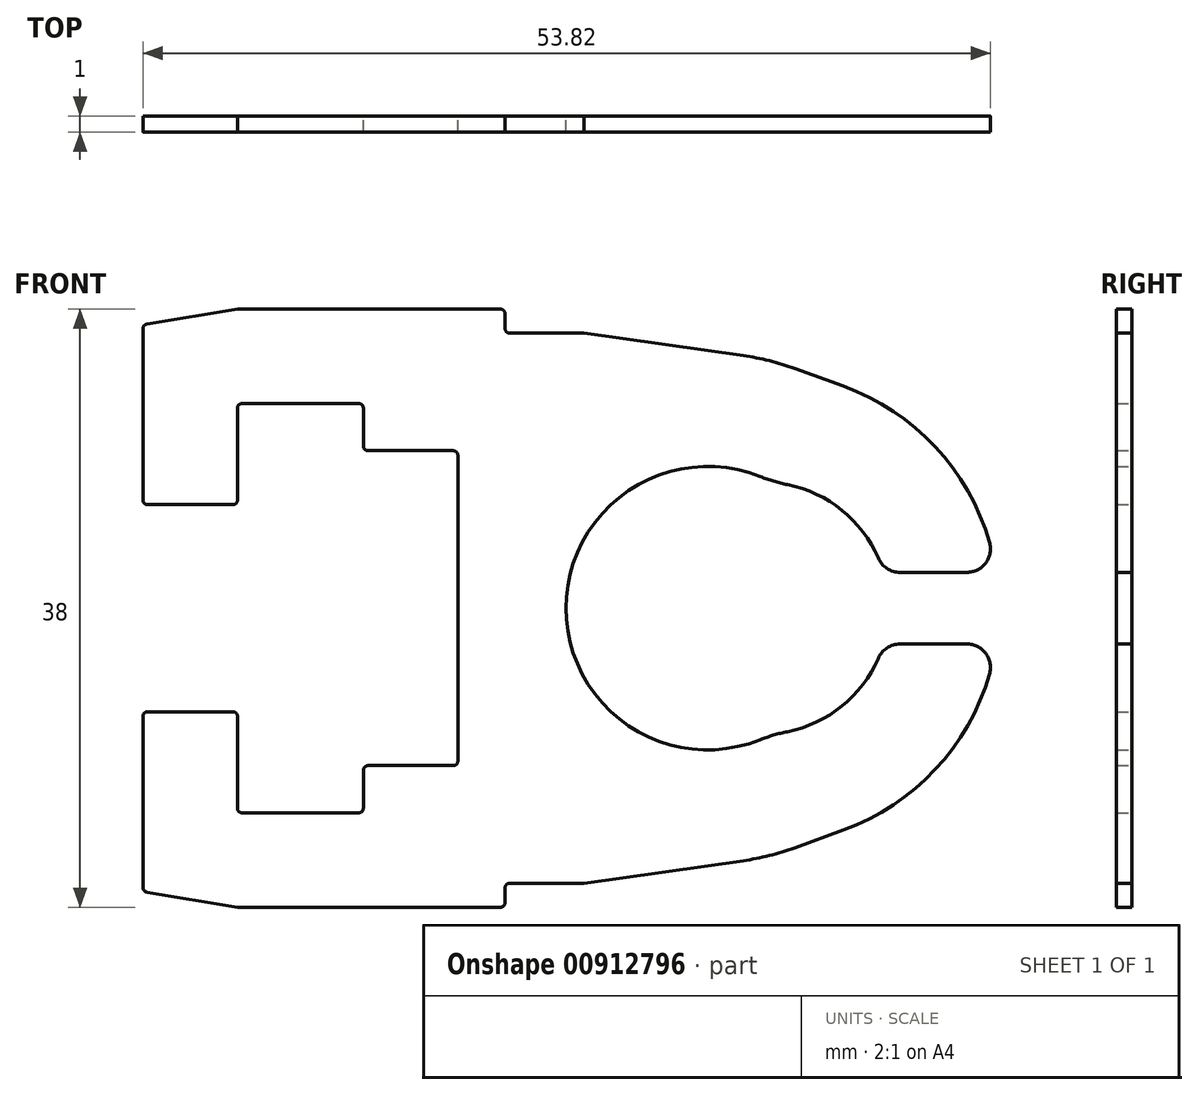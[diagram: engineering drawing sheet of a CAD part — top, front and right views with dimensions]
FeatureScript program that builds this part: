
annotation { "Feature Type Name" : "Feature", "Feature Type Description" : "" }
export const myFeature = defineFeature(function(context is Context, id is Id, definition is map)
    precondition{}
    {
        {
            var Q0;
            Q0=qCreatedBy(makeId("Front.planeOp"),FACE);
            var sketch = newSketch(context, id + "F0", { "sketchPlane" : qUnion([Q0])});
            skLineSegment(sketch, "E0", {"start": v(57.08, -14.1) * mm, "end": v(54, -15.22) * mm});
            skArc(sketch, "E1", {"start": v(50.71, -16.04) * mm, "mid": v(52.37, -15.72) * mm, "end": v(54, -15.22) * mm});
            skLineSegment(sketch, "E2", {"start": v(50.71, -16.04) * mm, "end": v(40.59, -17.47) * mm});
            skLineSegment(sketch, "E3", {"start": v(40.59, -17.47) * mm, "end": v(35.89, -17.47) * mm});
            skArc(sketch, "E4", {"start": v(35.89, -17.47) * mm, "mid": v(35.67, -17.55) * mm, "end": v(35.59, -17.77) * mm});
            skLineSegment(sketch, "E5", {"start": v(35.59, -17.77) * mm, "end": v(35.59, -18.7) * mm});
            skArc(sketch, "E6", {"start": v(35.29, -19) * mm, "mid": v(35.5, -18.91) * mm, "end": v(35.59, -18.7) * mm});
            skLineSegment(sketch, "E7", {"start": v(35.29, -19) * mm, "end": v(18.59, -19) * mm});
            skLineSegment(sketch, "E8", {"start": v(18.59, -19) * mm, "end": v(12.84, -18.04) * mm});
            skArc(sketch, "E9", {"start": v(12.59, -17.75) * mm, "mid": v(12.66, -17.94) * mm, "end": v(12.84, -18.04) * mm});
            skLineSegment(sketch, "E10", {"start": v(12.59, -17.75) * mm, "end": v(12.59, -6.87) * mm});
            skArc(sketch, "E11", {"start": v(12.89, -6.58) * mm, "mid": v(12.67, -6.66) * mm, "end": v(12.59, -6.88) * mm});
            skLineSegment(sketch, "E12", {"start": v(12.89, -6.58) * mm, "end": v(18.29, -6.58) * mm});
            skArc(sketch, "E13", {"start": v(18.59, -6.88) * mm, "mid": v(18.5, -6.66) * mm, "end": v(18.29, -6.58) * mm});
            skLineSegment(sketch, "E14", {"start": v(18.59, -6.88) * mm, "end": v(18.59, -12.7) * mm});
            skArc(sketch, "E15", {"start": v(18.59, -12.7) * mm, "mid": v(18.67, -12.91) * mm, "end": v(18.89, -13) * mm});
            skLineSegment(sketch, "E16", {"start": v(18.89, -13) * mm, "end": v(26.29, -13) * mm});
            skArc(sketch, "E17", {"start": v(26.29, -13) * mm, "mid": v(26.5, -12.91) * mm, "end": v(26.59, -12.7) * mm});
            skLineSegment(sketch, "E18", {"start": v(26.59, -12.7) * mm, "end": v(26.59, -10.3) * mm});
            skArc(sketch, "E19", {"start": v(26.89, -10) * mm, "mid": v(26.67, -10.09) * mm, "end": v(26.59, -10.3) * mm});
            skLineSegment(sketch, "E20", {"start": v(26.89, -10) * mm, "end": v(32.29, -10) * mm});
            skArc(sketch, "E21", {"start": v(32.29, -10) * mm, "mid": v(32.5, -9.91) * mm, "end": v(32.59, -9.7) * mm});
            skLineSegment(sketch, "E22", {"start": v(32.59, -9.7) * mm, "end": v(32.59, 9.7) * mm});
            skArc(sketch, "E23", {"start": v(32.59, 9.7) * mm, "mid": v(32.5, 9.91) * mm, "end": v(32.29, 10) * mm});
            skLineSegment(sketch, "E24", {"start": v(32.29, 10) * mm, "end": v(26.89, 10) * mm});
            skArc(sketch, "E25", {"start": v(26.59, 10.3) * mm, "mid": v(26.67, 10.09) * mm, "end": v(26.89, 10) * mm});
            skLineSegment(sketch, "E26", {"start": v(26.59, 10.3) * mm, "end": v(26.59, 12.7) * mm});
            skArc(sketch, "E27", {"start": v(26.59, 12.7) * mm, "mid": v(26.5, 12.91) * mm, "end": v(26.29, 13) * mm});
            skLineSegment(sketch, "E28", {"start": v(26.29, 13) * mm, "end": v(18.89, 13) * mm});
            skArc(sketch, "E29", {"start": v(18.89, 13) * mm, "mid": v(18.67, 12.91) * mm, "end": v(18.59, 12.7) * mm});
            skLineSegment(sketch, "E30", {"start": v(18.59, 12.7) * mm, "end": v(18.59, 6.88) * mm});
            skArc(sketch, "E31", {"start": v(18.29, 6.58) * mm, "mid": v(18.5, 6.66) * mm, "end": v(18.59, 6.88) * mm});
            skLineSegment(sketch, "E32", {"start": v(18.29, 6.57) * mm, "end": v(12.89, 6.57) * mm});
            skArc(sketch, "E33", {"start": v(12.59, 6.88) * mm, "mid": v(12.67, 6.66) * mm, "end": v(12.89, 6.58) * mm});
            skLineSegment(sketch, "E34", {"start": v(12.59, 6.88) * mm, "end": v(12.59, 17.75) * mm});
            skArc(sketch, "E35", {"start": v(12.84, 18.04) * mm, "mid": v(12.66, 17.94) * mm, "end": v(12.59, 17.75) * mm});
            skLineSegment(sketch, "E36", {"start": v(12.84, 18.04) * mm, "end": v(18.59, 19) * mm});
            skLineSegment(sketch, "E37", {"start": v(18.59, 19) * mm, "end": v(35.29, 19) * mm});
            skArc(sketch, "E38", {"start": v(35.59, 18.7) * mm, "mid": v(35.5, 18.91) * mm, "end": v(35.29, 19) * mm});
            skLineSegment(sketch, "E39", {"start": v(35.59, 18.7) * mm, "end": v(35.59, 17.76) * mm});
            skArc(sketch, "E40", {"start": v(35.59, 17.76) * mm, "mid": v(35.67, 17.55) * mm, "end": v(35.89, 17.46) * mm});
            skLineSegment(sketch, "E41", {"start": v(35.89, 17.46) * mm, "end": v(40.59, 17.46) * mm});
            skLineSegment(sketch, "E42", {"start": v(40.59, 17.46) * mm, "end": v(50.71, 16.04) * mm});
            skArc(sketch, "E43", {"start": v(54, 15.22) * mm, "mid": v(52.37, 15.72) * mm, "end": v(50.71, 16.04) * mm});
            skLineSegment(sketch, "E44", {"start": v(54, 15.22) * mm, "end": v(57.08, 14.1) * mm});
            skArc(sketch, "E45", {"start": v(66.35, 4.2) * mm, "mid": v(62.9, 10.25) * mm, "end": v(57.08, 14.1) * mm});
            skArc(sketch, "E46", {"start": v(64.91, 2.27) * mm, "mid": v(66.11, 2.87) * mm, "end": v(66.35, 4.2) * mm});
            skLineSegment(sketch, "E47", {"start": v(64.91, 2.27) * mm, "end": v(60.67, 2.27) * mm});
            skArc(sketch, "E48", {"start": v(59.3, 3.18) * mm, "mid": v(59.85, 2.52) * mm, "end": v(60.67, 2.27) * mm});
            skArc(sketch, "E49", {"start": v(59.3, 3.18) * mm, "mid": v(56.98, 6.22) * mm, "end": v(53.52, 7.84) * mm});
            skArc(sketch, "E50", {"start": v(51.79, 8.36) * mm, "mid": v(52.64, 8.06) * mm, "end": v(53.52, 7.84) * mm});
            skArc(sketch, "E51", {"start": v(51.79, 8.36) * mm, "mid": v(39.45, 0) * mm, "end": v(51.79, -8.36) * mm});
            skArc(sketch, "E52", {"start": v(53.52, -7.84) * mm, "mid": v(52.64, -8.06) * mm, "end": v(51.79, -8.36) * mm});
            skArc(sketch, "E53", {"start": v(53.52, -7.84) * mm, "mid": v(56.98, -6.22) * mm, "end": v(59.3, -3.18) * mm});
            skArc(sketch, "E54", {"start": v(60.67, -2.28) * mm, "mid": v(59.85, -2.52) * mm, "end": v(59.3, -3.18) * mm});
            skLineSegment(sketch, "E55", {"start": v(60.67, -2.28) * mm, "end": v(64.91, -2.28) * mm});
            skArc(sketch, "E56", {"start": v(66.35, -4.2) * mm, "mid": v(66.11, -2.87) * mm, "end": v(64.91, -2.28) * mm});
            skArc(sketch, "E57", {"start": v(57.08, -14.1) * mm, "mid": v(62.9, -10.25) * mm, "end": v(66.35, -4.2) * mm});
            skSolve(sketch);
        }
        {
            var Q0;
            Q0=makeQuery(id+"F0.imprint","IMPRINT",FACE,{"disambiguationData":[TD([[makeQuery(id+"F0.imprint","IMPRINT",EDGE,{"derivedFrom":sQuery(id+"F0.wireOp",EDGE,"E0")}),-1.0]])]});
            extrude(context, id + "F1", {"entities" : qUnion([Q0]), "endBound" : BoundingType.SYMMETRIC, "depth" : 1 * mm, "offsetDistance" : 25 * mm});
        }
    });
